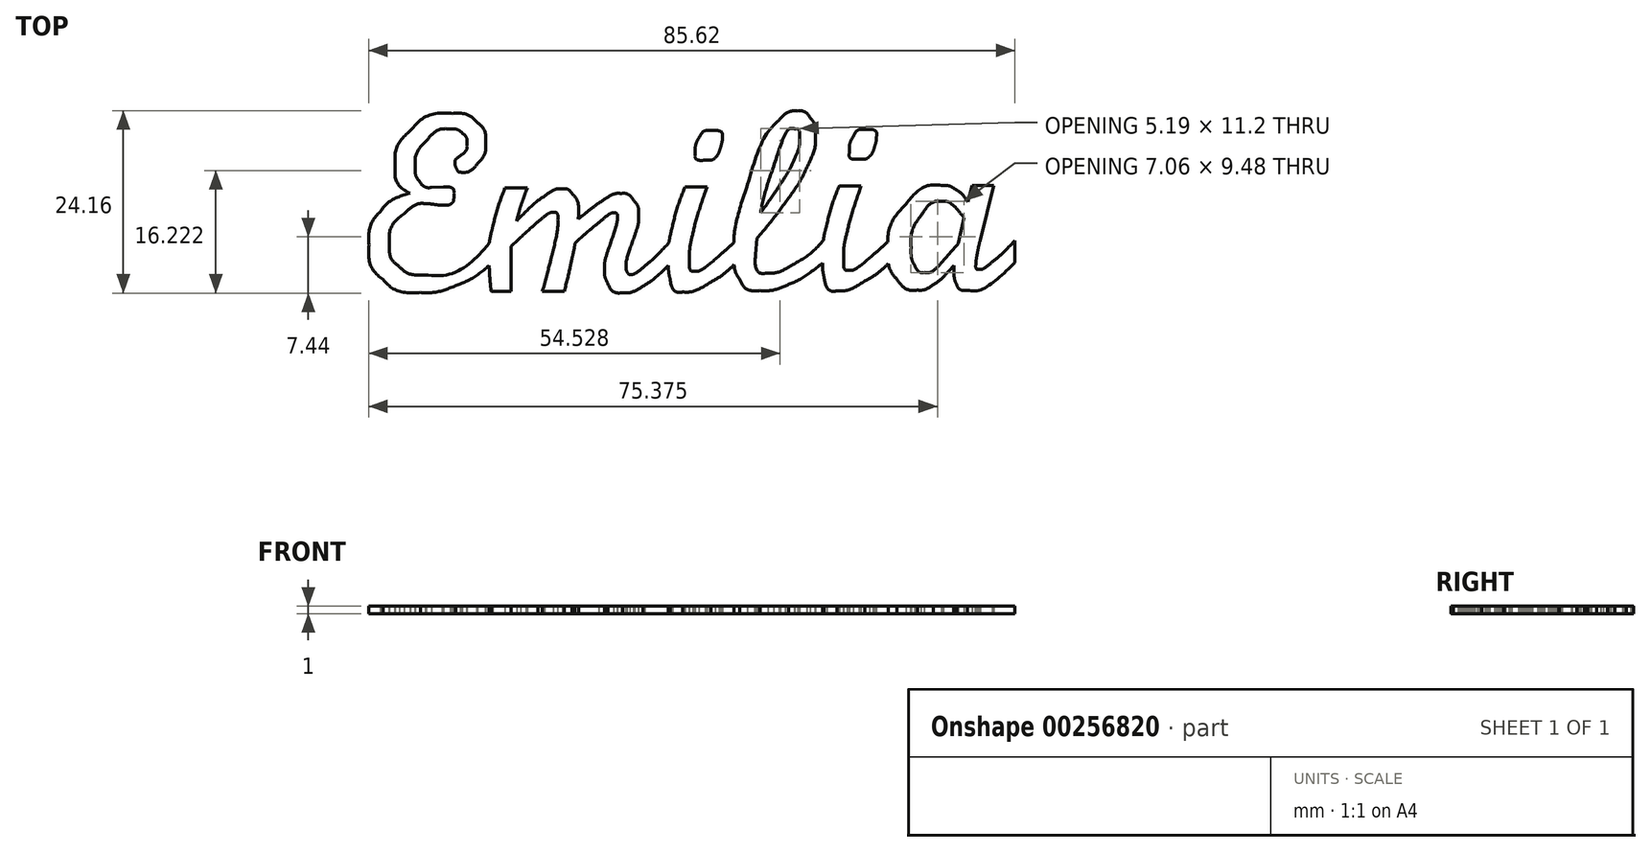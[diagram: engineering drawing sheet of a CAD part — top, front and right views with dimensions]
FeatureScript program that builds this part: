
annotation { "Feature Type Name" : "Feature", "Feature Type Description" : "" }
export const myFeature = defineFeature(function(context is Context, id is Id, definition is map)
    precondition{}
    {
        {
            var Q0;
            Q0=qCreatedBy(makeId("Top.planeOp"),FACE);
            var sketch = newSketch(context, id + "F0", { "sketchPlane" : qUnion([Q0])});
            skFitSpline(sketch, "E0", {"points": [v(-26.76, -8.32) * mm, v(-28.28, -9.56) * mm, v(-29.8, -10.5) * mm, v(-31.34, -11.12) * mm]});
            skFitSpline(sketch, "E1", {"points": [v(-31.34, -11.12) * mm, v(-32.88, -11.71) * mm, v(-34.42, -12.01) * mm, v(-35.96, -12.01) * mm]});
            skFitSpline(sketch, "E2", {"points": [v(-35.96, -12.01) * mm, v(-38.03, -12.01) * mm, v(-39.68, -11.44) * mm, v(-40.92, -10.29) * mm]});
            skFitSpline(sketch, "E3", {"points": [v(-40.92, -10.29) * mm, v(-42.16, -9.14) * mm, v(-42.78, -7.61) * mm, v(-42.78, -5.7) * mm]});
            skFitSpline(sketch, "E4", {"points": [v(-42.78, -5.7) * mm, v(-42.78, -3.94) * mm, v(-42.29, -2.47) * mm, v(-41.3, -1.3) * mm]});
            skFitSpline(sketch, "E5", {"points": [v(-41.3, -1.3) * mm, v(-40.4, -0.24) * mm, v(-39.1, 0.58) * mm, v(-37.37, 1.15) * mm]});
            skFitSpline(sketch, "E6", {"points": [v(-37.37, 1.15) * mm, v(-38.66, 2.02) * mm, v(-39.3, 3.27) * mm, v(-39.3, 4.9) * mm]});
            skFitSpline(sketch, "E7", {"points": [v(-39.3, 4.9) * mm, v(-39.3, 6.58) * mm, v(-38.64, 8.1) * mm, v(-37.3, 9.45) * mm]});
            skFitSpline(sketch, "E8", {"points": [v(-37.3, 9.45) * mm, v(-35.81, 10.97) * mm, v(-33.94, 11.73) * mm, v(-31.69, 11.73) * mm]});
            skFitSpline(sketch, "E9", {"points": [v(-31.69, 11.73) * mm, v(-30.38, 11.73) * mm, v(-29.33, 11.36) * mm, v(-28.55, 10.62) * mm]});
            skFitSpline(sketch, "E10", {"points": [v(-28.55, 10.62) * mm, v(-27.75, 9.91) * mm, v(-27.35, 8.97) * mm, v(-27.35, 7.8) * mm]});
            skFitSpline(sketch, "E11", {"points": [v(-27.35, 7.8) * mm, v(-27.35, 6.79) * mm, v(-27.7, 5.9) * mm, v(-28.38, 5.11) * mm]});
            skFitSpline(sketch, "E12", {"points": [v(-28.38, 5.11) * mm, v(-29.07, 4.33) * mm, v(-29.85, 3.94) * mm, v(-30.72, 3.94) * mm]});
            skFitSpline(sketch, "E13", {"points": [v(-30.72, 3.94) * mm, v(-30.86, 3.94) * mm, v(-31.01, 4.09) * mm, v(-31.17, 4.39) * mm]});
            skFitSpline(sketch, "E14", {"points": [v(-31.17, 4.39) * mm, v(-31.33, 4.7) * mm, v(-31.41, 5.05) * mm, v(-31.41, 5.42) * mm]});
            skFitSpline(sketch, "E15", {"points": [v(-31.41, 5.42) * mm, v(-31.41, 5.51) * mm, v(-31.15, 5.77) * mm, v(-30.62, 6.18) * mm]});
            skFitSpline(sketch, "E16", {"points": [v(-30.62, 6.18) * mm, v(-30.07, 6.62) * mm, v(-29.8, 7.12) * mm, v(-29.8, 7.7) * mm]});
            skFitSpline(sketch, "E17", {"points": [v(-29.8, 7.7) * mm, v(-29.8, 8.27) * mm, v(-30, 8.74) * mm, v(-30.41, 9.1) * mm]});
            skFitSpline(sketch, "E18", {"points": [v(-30.41, 9.1) * mm, v(-30.83, 9.48) * mm, v(-31.36, 9.66) * mm, v(-32, 9.66) * mm]});
            skFitSpline(sketch, "E19", {"points": [v(-32, 9.66) * mm, v(-33.17, 9.66) * mm, v(-34.24, 9.13) * mm, v(-35.2, 8.07) * mm]});
            skFitSpline(sketch, "E20", {"points": [v(-35.2, 8.07) * mm, v(-36.17, 7.02) * mm, v(-36.65, 5.85) * mm, v(-36.65, 4.56) * mm]});
            skFitSpline(sketch, "E21", {"points": [v(-36.65, 4.56) * mm, v(-36.65, 3.83) * mm, v(-36.45, 3.2) * mm, v(-36.06, 2.67) * mm]});
            skFitSpline(sketch, "E22", {"points": [v(-36.06, 2.67) * mm, v(-35.65, 2.16) * mm, v(-35.13, 1.9) * mm, v(-34.51, 1.9) * mm]});
            skLineSegment(sketch, "E23", {"start": v(-26.76, -5.4) * mm, "end": v(-26.76, -8.32) * mm});
            skLineSegment(sketch, "E24", {"start": v(-26.76, -8.32) * mm, "end": v(-26.76, -5.4) * mm});
            skFitSpline(sketch, "E25", {"points": [v(-32.93, 1.98) * mm, v(-32.33, 1.98) * mm, v(-31.95, 1.93) * mm, v(-31.8, 1.84) * mm]});
            skFitSpline(sketch, "E26", {"points": [v(-31.8, 1.84) * mm, v(-31.63, 1.75) * mm, v(-31.55, 1.53) * mm, v(-31.55, 1.18) * mm]});
            skFitSpline(sketch, "E27", {"points": [v(-31.55, 1.18) * mm, v(-31.55, 0.43) * mm, v(-31.65, -0.03) * mm, v(-31.86, -0.2) * mm]});
            skFitSpline(sketch, "E28", {"points": [v(-31.86, -0.2) * mm, v(-32.07, -0.35) * mm, v(-32.48, -0.44) * mm, v(-33.1, -0.44) * mm]});
            skFitSpline(sketch, "E29", {"points": [v(-33.1, -0.44) * mm, v(-33.33, -0.44) * mm, v(-33.69, -0.4) * mm, v(-34.17, -0.33) * mm]});
            skFitSpline(sketch, "E30", {"points": [v(-34.17, -0.33) * mm, v(-34.65, -0.26) * mm, v(-35.02, -0.23) * mm, v(-35.27, -0.23) * mm]});
            skFitSpline(sketch, "E31", {"points": [v(-35.27, -0.23) * mm, v(-36.14, -0.23) * mm, v(-37.1, -0.68) * mm, v(-38.13, -1.57) * mm]});
            skFitSpline(sketch, "E32", {"points": [v(-38.13, -1.57) * mm, v(-39.42, -2.67) * mm, v(-40.06, -4.03) * mm, v(-40.06, -5.64) * mm]});
            skFitSpline(sketch, "E33", {"points": [v(-40.06, -5.64) * mm, v(-40.06, -6.85) * mm, v(-39.64, -7.83) * mm, v(-38.79, -8.57) * mm]});
            skFitSpline(sketch, "E34", {"points": [v(-38.79, -8.57) * mm, v(-37.94, -9.3) * mm, v(-36.79, -9.67) * mm, v(-35.34, -9.67) * mm]});
            skFitSpline(sketch, "E35", {"points": [v(-35.34, -9.67) * mm, v(-32.42, -9.67) * mm, v(-29.56, -8.24) * mm, v(-26.76, -5.4) * mm]});
            skLineSegment(sketch, "E36", {"start": v(-34.51, 1.9) * mm, "end": v(-32.93, 1.98) * mm});
            skLineSegment(sketch, "E37", {"start": v(-32.93, 1.98) * mm, "end": v(-34.51, 1.9) * mm});
            skFitSpline(sketch, "E38", {"points": [v(-26.6, -11.87) * mm, v(-26.69, -11.12) * mm, v(-26.77, -10.17) * mm, v(-26.84, -9.05) * mm]});
            skFitSpline(sketch, "E39", {"points": [v(-26.84, -9.05) * mm, v(-26.88, -7.9) * mm, v(-26.9, -7.16) * mm, v(-26.9, -6.84) * mm]});
            skFitSpline(sketch, "E40", {"points": [v(-26.9, -6.84) * mm, v(-26.9, -5.88) * mm, v(-26.72, -4.65) * mm, v(-26.35, -3.16) * mm]});
            skFitSpline(sketch, "E41", {"points": [v(-26.35, -3.16) * mm, v(-25.99, -1.64) * mm, v(-25.46, 0.04) * mm, v(-24.77, 1.87) * mm]});
            skLineSegment(sketch, "E42", {"start": v(-23.94, -11.87) * mm, "end": v(-26.6, -11.87) * mm});
            skLineSegment(sketch, "E43", {"start": v(-26.6, -11.87) * mm, "end": v(-23.94, -11.87) * mm});
            skFitSpline(sketch, "E44", {"points": [v(-21.98, 1.4) * mm, v(-22.28, 0.59) * mm, v(-22.52, -0.08) * mm, v(-22.7, -0.6) * mm]});
            skFitSpline(sketch, "E45", {"points": [v(-22.7, -0.6) * mm, v(-22.86, -1.14) * mm, v(-23.04, -1.77) * mm, v(-23.22, -2.5) * mm]});
            skFitSpline(sketch, "E46", {"points": [v(-23.22, -2.5) * mm, v(-21.66, -0.94) * mm, v(-20.43, 0.15) * mm, v(-19.53, 0.77) * mm]});
            skFitSpline(sketch, "E47", {"points": [v(-19.53, 0.77) * mm, v(-18.61, 1.41) * mm, v(-17.82, 1.74) * mm, v(-17.16, 1.74) * mm]});
            skFitSpline(sketch, "E48", {"points": [v(-17.16, 1.74) * mm, v(-16.65, 1.74) * mm, v(-16.2, 1.48) * mm, v(-15.78, 0.98) * mm]});
            skFitSpline(sketch, "E49", {"points": [v(-15.78, 0.98) * mm, v(-15.27, 0.33) * mm, v(-15.02, -0.55) * mm, v(-15.02, -1.68) * mm]});
            skLineSegment(sketch, "E50", {"start": v(-24.77, 1.87) * mm, "end": v(-21.77, 1.87) * mm});
            skLineSegment(sketch, "E51", {"start": v(-21.77, 1.87) * mm, "end": v(-21.98, 1.4) * mm});
            skLineSegment(sketch, "E52", {"start": v(-21.98, 1.4) * mm, "end": v(-24.77, 1.87) * mm});
            skFitSpline(sketch, "E53", {"points": [v(-15.05, -2.26) * mm, v(-13.7, -1.18) * mm, v(-12.8, -0.48) * mm, v(-12.33, -0.16) * mm]});
            skFitSpline(sketch, "E54", {"points": [v(-12.33, -0.16) * mm, v(-11.07, 0.7) * mm, v(-10.08, 1.11) * mm, v(-9.37, 1.11) * mm]});
            skFitSpline(sketch, "E55", {"points": [v(-9.37, 1.11) * mm, v(-8.75, 1.11) * mm, v(-8.2, 0.83) * mm, v(-7.75, 0.25) * mm]});
            skFitSpline(sketch, "E56", {"points": [v(-7.75, 0.25) * mm, v(-7.3, -0.32) * mm, v(-7.06, -1.02) * mm, v(-7.06, -1.85) * mm]});
            skFitSpline(sketch, "E57", {"points": [v(-7.06, -1.85) * mm, v(-7.06, -2.56) * mm, v(-7.23, -3.4) * mm, v(-7.58, -4.4) * mm]});
            skFitSpline(sketch, "E58", {"points": [v(-7.58, -4.4) * mm, v(-8.34, -6.6) * mm, v(-8.71, -8) * mm, v(-8.71, -8.6) * mm]});
            skFitSpline(sketch, "E59", {"points": [v(-8.71, -8.6) * mm, v(-8.71, -8.88) * mm, v(-8.67, -9.12) * mm, v(-8.58, -9.32) * mm]});
            skFitSpline(sketch, "E60", {"points": [v(-8.58, -9.32) * mm, v(-8.46, -9.5) * mm, v(-8.34, -9.6) * mm, v(-8.2, -9.6) * mm]});
            skFitSpline(sketch, "E61", {"points": [v(-8.2, -9.6) * mm, v(-7.78, -9.6) * mm, v(-7.13, -9.23) * mm, v(-6.23, -8.5) * mm]});
            skFitSpline(sketch, "E62", {"points": [v(-6.23, -8.5) * mm, v(-5.34, -7.74) * mm, v(-4.27, -6.7) * mm, v(-3.03, -5.4) * mm]});
            skLineSegment(sketch, "E63", {"start": v(-15.02, -1.68) * mm, "end": v(-15.05, -2.26) * mm});
            skLineSegment(sketch, "E64", {"start": v(-15.05, -2.26) * mm, "end": v(-15.02, -1.68) * mm});
            skFitSpline(sketch, "E65", {"points": [v(-3.03, -8.32) * mm, v(-4.34, -9.61) * mm, v(-5.49, -10.55) * mm, v(-6.48, -11.15) * mm]});
            skFitSpline(sketch, "E66", {"points": [v(-6.48, -11.15) * mm, v(-7.44, -11.75) * mm, v(-8.34, -12.05) * mm, v(-9.16, -12.05) * mm]});
            skFitSpline(sketch, "E67", {"points": [v(-9.16, -12.05) * mm, v(-10.06, -12.05) * mm, v(-10.72, -11.62) * mm, v(-11.16, -10.77) * mm]});
            skFitSpline(sketch, "E68", {"points": [v(-11.16, -10.77) * mm, v(-11.44, -10.22) * mm, v(-11.57, -9.63) * mm, v(-11.57, -9.01) * mm]});
            skFitSpline(sketch, "E69", {"points": [v(-11.57, -9.01) * mm, v(-11.57, -8.23) * mm, v(-11.4, -7.33) * mm, v(-11.06, -6.3) * mm]});
            skFitSpline(sketch, "E70", {"points": [v(-11.06, -6.3) * mm, v(-10.28, -3.95) * mm, v(-9.89, -2.55) * mm, v(-9.89, -2.09) * mm]});
            skFitSpline(sketch, "E71", {"points": [v(-9.89, -2.09) * mm, v(-9.89, -1.68) * mm, v(-10.05, -1.47) * mm, v(-10.37, -1.47) * mm]});
            skFitSpline(sketch, "E72", {"points": [v(-10.37, -1.47) * mm, v(-10.67, -1.47) * mm, v(-11.48, -2.02) * mm, v(-12.81, -3.12) * mm]});
            skFitSpline(sketch, "E73", {"points": [v(-12.81, -3.12) * mm, v(-13.55, -3.74) * mm, v(-14.27, -4.36) * mm, v(-14.99, -4.98) * mm]});
            skLineSegment(sketch, "E74", {"start": v(-3.03, -5.4) * mm, "end": v(-3.03, -8.32) * mm});
            skLineSegment(sketch, "E75", {"start": v(-3.03, -8.32) * mm, "end": v(-3.03, -5.4) * mm});
            skFitSpline(sketch, "E76", {"points": [v(-15.5, -5.5) * mm, v(-15.57, -6) * mm, v(-15.7, -6.7) * mm, v(-15.92, -7.6) * mm]});
            skFitSpline(sketch, "E77", {"points": [v(-15.92, -7.6) * mm, v(-16.1, -8.5) * mm, v(-16.43, -9.92) * mm, v(-16.91, -11.87) * mm]});
            skLineSegment(sketch, "E78", {"start": v(-14.99, -4.98) * mm, "end": v(-15.5, -5.5) * mm});
            skLineSegment(sketch, "E79", {"start": v(-15.5, -5.5) * mm, "end": v(-14.99, -4.98) * mm});
            skFitSpline(sketch, "E80", {"points": [v(-19.8, -11.87) * mm, v(-19.17, -9.46) * mm, v(-18.75, -7.89) * mm, v(-18.57, -7.15) * mm]});
            skFitSpline(sketch, "E81", {"points": [v(-18.57, -7.15) * mm, v(-18.04, -4.95) * mm, v(-17.78, -3.35) * mm, v(-17.78, -2.36) * mm]});
            skFitSpline(sketch, "E82", {"points": [v(-17.78, -2.36) * mm, v(-17.78, -1.72) * mm, v(-17.97, -1.4) * mm, v(-18.36, -1.4) * mm]});
            skFitSpline(sketch, "E83", {"points": [v(-18.36, -1.4) * mm, v(-18.73, -1.4) * mm, v(-19.4, -1.81) * mm, v(-20.4, -2.64) * mm]});
            skFitSpline(sketch, "E84", {"points": [v(-20.4, -2.64) * mm, v(-21.13, -3.26) * mm, v(-22.31, -4.34) * mm, v(-23.94, -5.88) * mm]});
            skLineSegment(sketch, "E85", {"start": v(-16.91, -11.87) * mm, "end": v(-19.8, -11.87) * mm});
            skLineSegment(sketch, "E86", {"start": v(-19.8, -11.87) * mm, "end": v(-16.91, -11.87) * mm});
            skLineSegment(sketch, "E87", {"start": v(-23.94, -5.88) * mm, "end": v(-24.01, -8.19) * mm});
            skLineSegment(sketch, "E88", {"start": v(-24.01, -8.19) * mm, "end": v(-23.94, -11.87) * mm});
            skLineSegment(sketch, "E89", {"start": v(-23.94, -11.87) * mm, "end": v(-23.94, -5.88) * mm});
            skFitSpline(sketch, "E90", {"points": [v(5.7, -8.18) * mm, v(4.8, -9.08) * mm, v(3.74, -9.9) * mm, v(2.5, -10.63) * mm]});
            skFitSpline(sketch, "E91", {"points": [v(2.5, -10.63) * mm, v(1.03, -11.5) * mm, v(-0.21, -11.94) * mm, v(-1.22, -11.94) * mm]});
            skFitSpline(sketch, "E92", {"points": [v(-1.22, -11.94) * mm, v(-2.07, -11.94) * mm, v(-2.64, -11.34) * mm, v(-2.91, -10.15) * mm]});
            skFitSpline(sketch, "E93", {"points": [v(-2.91, -10.15) * mm, v(-3.05, -9.55) * mm, v(-3.12, -8.6) * mm, v(-3.12, -7.32) * mm]});
            skFitSpline(sketch, "E94", {"points": [v(-3.12, -7.32) * mm, v(-3.12, -6.08) * mm, v(-2.92, -4.66) * mm, v(-2.53, -3.05) * mm]});
            skFitSpline(sketch, "E95", {"points": [v(-2.53, -3.05) * mm, v(-2.14, -1.44) * mm, v(-1.6, 0.24) * mm, v(-0.91, 1.98) * mm]});
            skLineSegment(sketch, "E96", {"start": v(5.7, -5.25) * mm, "end": v(5.7, -8.18) * mm});
            skLineSegment(sketch, "E97", {"start": v(5.7, -8.18) * mm, "end": v(5.7, -5.25) * mm});
            skFitSpline(sketch, "E98", {"points": [v(1.64, 0.95) * mm, v(0.92, -1.19) * mm, v(0.42, -2.9) * mm, v(0.12, -4.19) * mm]});
            skFitSpline(sketch, "E99", {"points": [v(0.12, -4.19) * mm, v(-0.18, -5.47) * mm, v(-0.33, -6.59) * mm, v(-0.33, -7.53) * mm]});
            skFitSpline(sketch, "E100", {"points": [v(-0.33, -7.53) * mm, v(-0.33, -8.63) * mm, v(-0.1, -9.18) * mm, v(0.33, -9.18) * mm]});
            skFitSpline(sketch, "E101", {"points": [v(0.33, -9.18) * mm, v(0.9, -9.18) * mm, v(2, -8.5) * mm, v(3.63, -7.11) * mm]});
            skFitSpline(sketch, "E102", {"points": [v(3.63, -7.11) * mm, v(4.32, -6.52) * mm, v(5.01, -5.9) * mm, v(5.7, -5.25) * mm]});
            skLineSegment(sketch, "E103", {"start": v(-0.91, 1.98) * mm, "end": v(1.98, 1.98) * mm});
            skLineSegment(sketch, "E104", {"start": v(1.98, 1.98) * mm, "end": v(1.64, 0.95) * mm});
            skLineSegment(sketch, "E105", {"start": v(1.64, 0.95) * mm, "end": v(-0.91, 1.98) * mm});
            skFitSpline(sketch, "E106", {"points": [v(2.32, 9.46) * mm, v(3.45, 9.46) * mm, v(4.01, 9.14) * mm, v(4.01, 8.5) * mm]});
            skFitSpline(sketch, "E107", {"points": [v(4.01, 8.5) * mm, v(4.01, 8.12) * mm, v(3.92, 7.65) * mm, v(3.74, 7.08) * mm]});
            skFitSpline(sketch, "E108", {"points": [v(3.74, 7.08) * mm, v(3.55, 6.53) * mm, v(3.34, 6.13) * mm, v(3.08, 5.87) * mm]});
            skFitSpline(sketch, "E109", {"points": [v(3.08, 5.87) * mm, v(2.85, 5.64) * mm, v(2.4, 5.53) * mm, v(1.74, 5.53) * mm]});
            skFitSpline(sketch, "E110", {"points": [v(1.74, 5.53) * mm, v(0.87, 5.53) * mm, v(0.43, 5.82) * mm, v(0.43, 6.4) * mm]});
            skFitSpline(sketch, "E111", {"points": [v(0.43, 6.4) * mm, v(0.43, 7.2) * mm, v(0.6, 7.9) * mm, v(0.95, 8.53) * mm]});
            skFitSpline(sketch, "E112", {"points": [v(0.95, 8.53) * mm, v(1.31, 9.15) * mm, v(1.77, 9.46) * mm, v(2.32, 9.46) * mm]});
            skFitSpline(sketch, "E113", {"points": [v(17.4, -8.04) * mm, v(15.63, -9.4) * mm, v(14.1, -10.36) * mm, v(12.81, -10.93) * mm]});
            skFitSpline(sketch, "E114", {"points": [v(12.81, -10.93) * mm, v(11.53, -11.48) * mm, v(10.26, -11.76) * mm, v(9.02, -11.76) * mm]});
            skFitSpline(sketch, "E115", {"points": [v(9.02, -11.76) * mm, v(7.78, -11.76) * mm, v(6.88, -11.25) * mm, v(6.3, -10.24) * mm]});
            skFitSpline(sketch, "E116", {"points": [v(6.3, -10.24) * mm, v(5.82, -9.42) * mm, v(5.58, -8.32) * mm, v(5.58, -6.94) * mm]});
            skFitSpline(sketch, "E117", {"points": [v(5.58, -6.94) * mm, v(5.58, -4.55) * mm, v(6.18, -1.46) * mm, v(7.37, 2.33) * mm]});
            skFitSpline(sketch, "E118", {"points": [v(7.37, 2.33) * mm, v(8.66, 6.4) * mm, v(10.03, 9.23) * mm, v(11.5, 10.84) * mm]});
            skFitSpline(sketch, "E119", {"points": [v(11.5, 10.84) * mm, v(12.33, 11.64) * mm, v(13.16, 12.05) * mm, v(13.98, 12.05) * mm]});
            skFitSpline(sketch, "E120", {"points": [v(13.98, 12.05) * mm, v(14.65, 12.05) * mm, v(15.21, 11.75) * mm, v(15.67, 11.15) * mm]});
            skFitSpline(sketch, "E121", {"points": [v(15.67, 11.15) * mm, v(16.13, 10.58) * mm, v(16.36, 9.85) * mm, v(16.36, 8.98) * mm]});
            skFitSpline(sketch, "E122", {"points": [v(16.36, 8.98) * mm, v(16.36, 7.67) * mm, v(15.98, 6.21) * mm, v(15.22, 4.6) * mm]});
            skFitSpline(sketch, "E123", {"points": [v(15.22, 4.6) * mm, v(14.58, 3.23) * mm, v(13.62, 1.65) * mm, v(12.33, -0.12) * mm]});
            skFitSpline(sketch, "E124", {"points": [v(12.33, -0.12) * mm, v(11.41, -1.4) * mm, v(10.17, -2.98) * mm, v(8.61, -4.84) * mm]});
            skLineSegment(sketch, "E125", {"start": v(17.4, -5.11) * mm, "end": v(17.4, -8.04) * mm});
            skLineSegment(sketch, "E126", {"start": v(17.4, -8.04) * mm, "end": v(17.4, -5.11) * mm});
            skFitSpline(sketch, "E127", {"points": [v(8.44, -6.94) * mm, v(8.44, -8.6) * mm, v(8.98, -9.42) * mm, v(10.06, -9.42) * mm]});
            skFitSpline(sketch, "E128", {"points": [v(10.06, -9.42) * mm, v(10.98, -9.42) * mm, v(12.14, -9.02) * mm, v(13.54, -8.21) * mm]});
            skFitSpline(sketch, "E129", {"points": [v(13.54, -8.21) * mm, v(14.94, -7.4) * mm, v(16.22, -6.37) * mm, v(17.4, -5.11) * mm]});
            skLineSegment(sketch, "E130", {"start": v(8.61, -4.84) * mm, "end": v(8.44, -6.94) * mm});
            skLineSegment(sketch, "E131", {"start": v(8.44, -6.94) * mm, "end": v(8.61, -4.84) * mm});
            skFitSpline(sketch, "E132", {"points": [v(9.1, -1.46) * mm, v(10.38, 0.35) * mm, v(11.26, 1.64) * mm, v(11.75, 2.4) * mm]});
            skFitSpline(sketch, "E133", {"points": [v(11.75, 2.4) * mm, v(12.57, 3.69) * mm, v(13.2, 4.81) * mm, v(13.6, 5.78) * mm]});
            skFitSpline(sketch, "E134", {"points": [v(13.6, 5.78) * mm, v(14.04, 6.76) * mm, v(14.26, 7.67) * mm, v(14.26, 8.5) * mm]});
            skFitSpline(sketch, "E135", {"points": [v(14.26, 8.5) * mm, v(14.26, 9.28) * mm, v(14.05, 9.67) * mm, v(13.64, 9.67) * mm]});
            skFitSpline(sketch, "E136", {"points": [v(13.64, 9.67) * mm, v(12.88, 9.67) * mm, v(11.94, 8.01) * mm, v(10.82, 4.7) * mm]});
            skFitSpline(sketch, "E137", {"points": [v(10.82, 4.7) * mm, v(10.01, 2.32) * mm, v(9.44, 0.26) * mm, v(9.1, -1.46) * mm]});
            skFitSpline(sketch, "E138", {"points": [v(26.13, -8.04) * mm, v(25.23, -8.94) * mm, v(24.16, -9.75) * mm, v(22.92, -10.49) * mm]});
            skFitSpline(sketch, "E139", {"points": [v(22.92, -10.49) * mm, v(21.45, -11.36) * mm, v(20.21, -11.8) * mm, v(19.2, -11.8) * mm]});
            skFitSpline(sketch, "E140", {"points": [v(19.2, -11.8) * mm, v(18.35, -11.8) * mm, v(17.79, -11.2) * mm, v(17.51, -10) * mm]});
            skFitSpline(sketch, "E141", {"points": [v(17.51, -10) * mm, v(17.38, -9.4) * mm, v(17.3, -8.46) * mm, v(17.3, -7.18) * mm]});
            skFitSpline(sketch, "E142", {"points": [v(17.3, -7.18) * mm, v(17.3, -5.94) * mm, v(17.5, -4.51) * mm, v(17.9, -2.9) * mm]});
            skFitSpline(sketch, "E143", {"points": [v(17.9, -2.9) * mm, v(18.28, -1.3) * mm, v(18.82, 0.38) * mm, v(19.51, 2.12) * mm]});
            skLineSegment(sketch, "E144", {"start": v(26.13, -5.11) * mm, "end": v(26.13, -8.04) * mm});
            skLineSegment(sketch, "E145", {"start": v(26.13, -8.04) * mm, "end": v(26.13, -5.11) * mm});
            skFitSpline(sketch, "E146", {"points": [v(22.06, 1.09) * mm, v(21.35, -1.05) * mm, v(20.84, -2.76) * mm, v(20.55, -4.04) * mm]});
            skFitSpline(sketch, "E147", {"points": [v(20.55, -4.04) * mm, v(20.25, -5.33) * mm, v(20.1, -6.44) * mm, v(20.1, -7.38) * mm]});
            skFitSpline(sketch, "E148", {"points": [v(20.1, -7.38) * mm, v(20.1, -8.49) * mm, v(20.32, -9.04) * mm, v(20.75, -9.04) * mm]});
            skFitSpline(sketch, "E149", {"points": [v(20.75, -9.04) * mm, v(21.33, -9.04) * mm, v(22.43, -8.35) * mm, v(24.06, -6.97) * mm]});
            skFitSpline(sketch, "E150", {"points": [v(24.06, -6.97) * mm, v(24.75, -6.37) * mm, v(25.44, -5.75) * mm, v(26.13, -5.11) * mm]});
            skLineSegment(sketch, "E151", {"start": v(19.51, 2.12) * mm, "end": v(22.4, 2.12) * mm});
            skLineSegment(sketch, "E152", {"start": v(22.4, 2.12) * mm, "end": v(22.06, 1.09) * mm});
            skLineSegment(sketch, "E153", {"start": v(22.06, 1.09) * mm, "end": v(19.51, 2.12) * mm});
            skFitSpline(sketch, "E154", {"points": [v(22.75, 9.6) * mm, v(23.88, 9.6) * mm, v(24.44, 9.28) * mm, v(24.44, 8.63) * mm]});
            skFitSpline(sketch, "E155", {"points": [v(24.44, 8.63) * mm, v(24.44, 8.27) * mm, v(24.35, 7.8) * mm, v(24.16, 7.22) * mm]});
            skFitSpline(sketch, "E156", {"points": [v(24.16, 7.22) * mm, v(23.98, 6.67) * mm, v(23.76, 6.27) * mm, v(23.5, 6.02) * mm]});
            skFitSpline(sketch, "E157", {"points": [v(23.5, 6.02) * mm, v(23.28, 5.79) * mm, v(22.83, 5.67) * mm, v(22.17, 5.67) * mm]});
            skFitSpline(sketch, "E158", {"points": [v(22.17, 5.67) * mm, v(21.3, 5.67) * mm, v(20.86, 5.96) * mm, v(20.86, 6.53) * mm]});
            skFitSpline(sketch, "E159", {"points": [v(20.86, 6.53) * mm, v(20.86, 7.34) * mm, v(21.03, 8.05) * mm, v(21.37, 8.67) * mm]});
            skFitSpline(sketch, "E160", {"points": [v(21.37, 8.67) * mm, v(21.74, 9.29) * mm, v(22.2, 9.6) * mm, v(22.75, 9.6) * mm]});
            skFitSpline(sketch, "E161", {"points": [v(42.78, -8.04) * mm, v(40.12, -10.5) * mm, v(38.03, -11.73) * mm, v(36.51, -11.73) * mm]});
            skFitSpline(sketch, "E162", {"points": [v(36.51, -11.73) * mm, v(35.8, -11.73) * mm, v(35.32, -11.46) * mm, v(35.07, -10.93) * mm]});
            skFitSpline(sketch, "E163", {"points": [v(35.07, -10.93) * mm, v(34.84, -10.38) * mm, v(34.72, -9.74) * mm, v(34.72, -9) * mm]});
            skLineSegment(sketch, "E164", {"start": v(42.78, -5.11) * mm, "end": v(42.78, -8.04) * mm});
            skLineSegment(sketch, "E165", {"start": v(42.78, -8.04) * mm, "end": v(42.78, -5.11) * mm});
            skFitSpline(sketch, "E166", {"points": [v(34.72, -8.42) * mm, v(33.62, -9.64) * mm, v(32.7, -10.49) * mm, v(31.96, -10.97) * mm]});
            skFitSpline(sketch, "E167", {"points": [v(31.96, -10.97) * mm, v(31.25, -11.45) * mm, v(30.55, -11.7) * mm, v(29.86, -11.7) * mm]});
            skFitSpline(sketch, "E168", {"points": [v(29.86, -11.7) * mm, v(28.83, -11.7) * mm, v(27.92, -11.2) * mm, v(27.14, -10.24) * mm]});
            skFitSpline(sketch, "E169", {"points": [v(27.14, -10.24) * mm, v(26.38, -9.26) * mm, v(26, -8.1) * mm, v(26, -6.76) * mm]});
            skFitSpline(sketch, "E170", {"points": [v(26, -6.76) * mm, v(26, -4.28) * mm, v(26.79, -2.14) * mm, v(28.35, -0.32) * mm]});
            skFitSpline(sketch, "E171", {"points": [v(28.35, -0.32) * mm, v(29.8, 1.35) * mm, v(31.37, 2.2) * mm, v(33.07, 2.2) * mm]});
            skFitSpline(sketch, "E172", {"points": [v(33.07, 2.2) * mm, v(33.76, 2.2) * mm, v(34.38, 2) * mm, v(34.93, 1.64) * mm]});
            skFitSpline(sketch, "E173", {"points": [v(34.93, 1.64) * mm, v(35.5, 1.3) * mm, v(36.04, 0.75) * mm, v(36.55, -0.01) * mm]});
            skLineSegment(sketch, "E174", {"start": v(34.72, -9) * mm, "end": v(34.72, -8.42) * mm});
            skLineSegment(sketch, "E175", {"start": v(34.72, -8.42) * mm, "end": v(34.72, -9) * mm});
            skFitSpline(sketch, "E176", {"points": [v(38.2, -5.08) * mm, v(38.04, -5.65) * mm, v(37.9, -6.27) * mm, v(37.79, -6.94) * mm]});
            skFitSpline(sketch, "E177", {"points": [v(37.79, -6.94) * mm, v(37.67, -7.58) * mm, v(37.61, -8.03) * mm, v(37.61, -8.28) * mm]});
            skFitSpline(sketch, "E178", {"points": [v(37.61, -8.28) * mm, v(37.61, -8.72) * mm, v(37.75, -8.94) * mm, v(38.03, -8.94) * mm]});
            skFitSpline(sketch, "E179", {"points": [v(38.03, -8.94) * mm, v(38.4, -8.94) * mm, v(39, -8.6) * mm, v(39.82, -7.94) * mm]});
            skFitSpline(sketch, "E180", {"points": [v(39.82, -7.94) * mm, v(40.67, -7.25) * mm, v(41.66, -6.3) * mm, v(42.78, -5.11) * mm]});
            skLineSegment(sketch, "E181", {"start": v(36.55, -0.01) * mm, "end": v(37.13, 2.16) * mm});
            skLineSegment(sketch, "E182", {"start": v(37.13, 2.16) * mm, "end": v(40, 2.16) * mm});
            skLineSegment(sketch, "E183", {"start": v(40, 2.16) * mm, "end": v(38.2, -5.08) * mm});
            skLineSegment(sketch, "E184", {"start": v(38.2, -5.08) * mm, "end": v(36.55, -0.01) * mm});
            skFitSpline(sketch, "E185", {"points": [v(36.06, -2.08) * mm, v(35.28, -1.16) * mm, v(34.77, -0.6) * mm, v(34.51, -0.4) * mm]});
            skFitSpline(sketch, "E186", {"points": [v(34.51, -0.4) * mm, v(34.15, -0.1) * mm, v(33.76, 0.06) * mm, v(33.34, 0.06) * mm]});
            skFitSpline(sketch, "E187", {"points": [v(33.34, 0.06) * mm, v(32.24, 0.06) * mm, v(31.24, -0.58) * mm, v(30.35, -1.84) * mm]});
            skFitSpline(sketch, "E188", {"points": [v(30.35, -1.84) * mm, v(29.47, -3.08) * mm, v(29.04, -4.48) * mm, v(29.04, -6.04) * mm]});
            skFitSpline(sketch, "E189", {"points": [v(29.04, -6.04) * mm, v(29.04, -7.03) * mm, v(29.2, -7.83) * mm, v(29.52, -8.45) * mm]});
            skFitSpline(sketch, "E190", {"points": [v(29.52, -8.45) * mm, v(29.84, -9.05) * mm, v(30.27, -9.35) * mm, v(30.8, -9.35) * mm]});
            skFitSpline(sketch, "E191", {"points": [v(30.8, -9.35) * mm, v(31.48, -9.35) * mm, v(32.3, -8.84) * mm, v(33.27, -7.83) * mm]});
            skFitSpline(sketch, "E192", {"points": [v(33.27, -7.83) * mm, v(33.94, -7.07) * mm, v(34.6, -6.3) * mm, v(35.27, -5.52) * mm]});
            skLineSegment(sketch, "E193", {"start": v(35.27, -5.52) * mm, "end": v(36.06, -2.08) * mm});
            skLineSegment(sketch, "E194", {"start": v(36.06, -2.08) * mm, "end": v(35.27, -5.52) * mm});
            skSolve(sketch);
        }
        {
            var Q0;
            Q0 = qSketchRegion(id + "F0", true);
            extrude(context, id + "F1", {"entities" : qUnion([Q0]), "depth" : 1 * mm});
        }
    });
